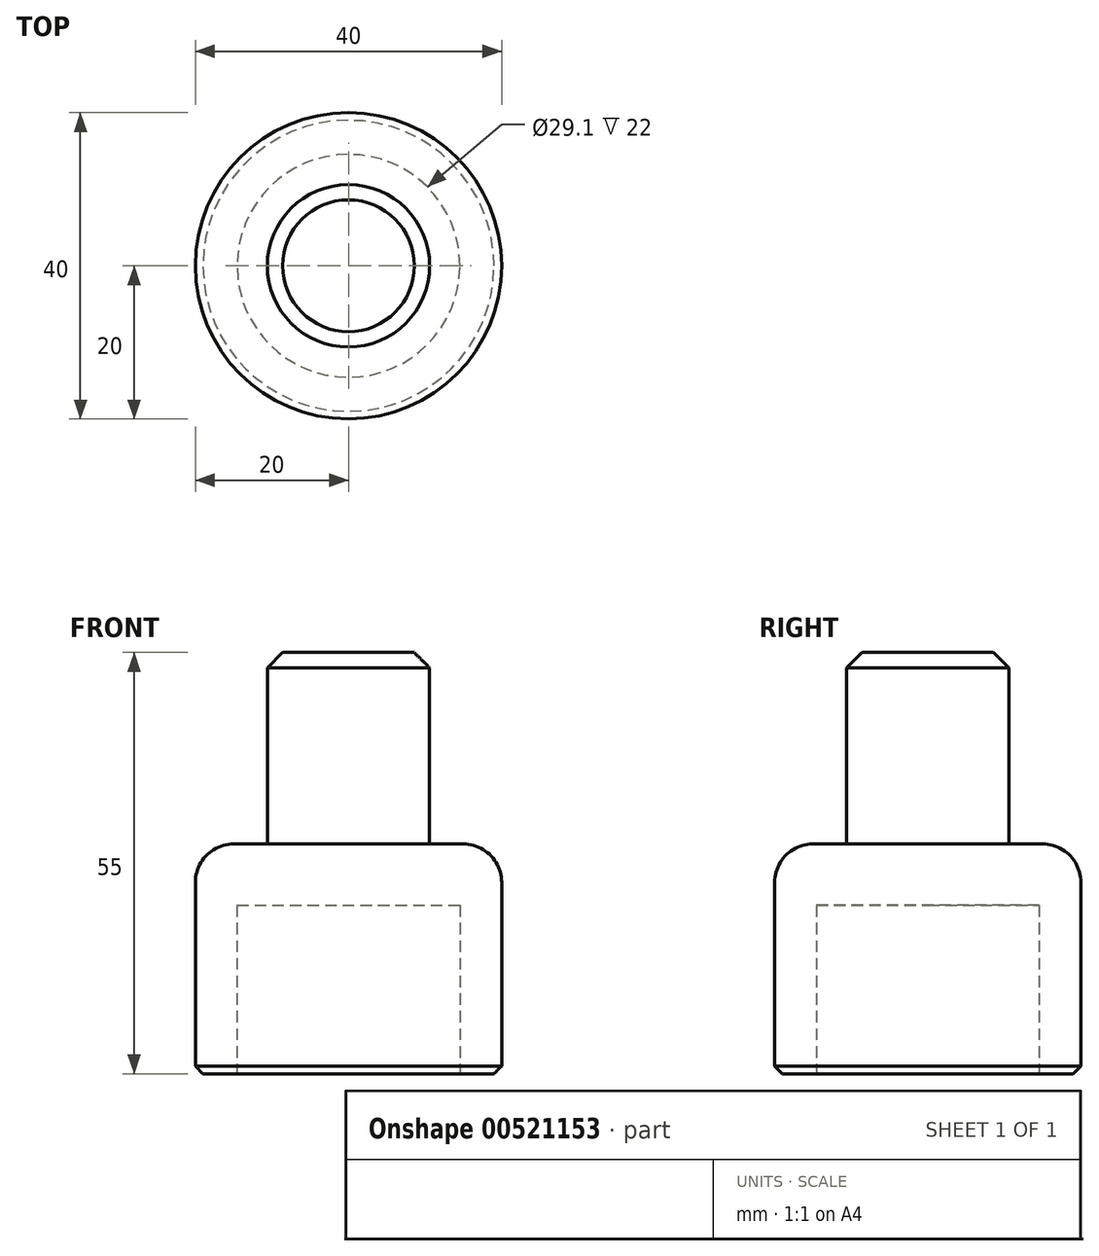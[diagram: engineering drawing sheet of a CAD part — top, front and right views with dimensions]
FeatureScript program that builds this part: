
annotation { "Feature Type Name" : "Feature", "Feature Type Description" : "" }
export const myFeature = defineFeature(function(context is Context, id is Id, definition is map)
    precondition{}
    {
        {
            var Q0;
            Q0=qCreatedBy(makeId("Top.planeOp"),FACE);
            var sketch = newSketch(context, id + "F0", { "sketchPlane" : qUnion([Q0])});
            skCircle(sketch, "E0", {"center": v(0, 0) * mm, "radius": 20 * mm});
            skSolve(sketch);
        }
        {
            var Q0;
            Q0 = qSketchRegion(id + "F0", true);
            extrude(context, id + "F1", {"entities" : qUnion([Q0]), "oppositeDirection" : true, "depth" : 30 * mm, "offsetDistance" : 25 * mm});
        }
        {
            var Q0;
            Q0=qCreatedBy(makeId("Top.planeOp"),FACE);
            var sketch = newSketch(context, id + "F2", { "sketchPlane" : qUnion([Q0])});
            skCircle(sketch, "E1", {"center": v(0, 0) * mm, "radius": 10.6 * mm});
            skSolve(sketch);
        }
        {
            var Q0;
            Q0 = qSketchRegion(id + "F2", true);
            extrude(context, id + "F3", {"entities" : qUnion([Q0]), "depth" : 25 * mm, "offsetDistance" : 25 * mm});
        }
        {
            var Q0;
            Q0=makeQuery(id+"F1.opExtrude","CAP_FACE",FACE,{"disambiguationData":[OSD([sQuery(id+"F0.wireOp",EDGE,"E0")])],"isStart":false});
            cPlane(context, id + "F4", {"entities" : qUnion([Q0]), "cplaneType" : CPlaneType.OFFSET, "offset" : 0 * mm, "width" : 150 * mm, "height" : 150 * mm});
        }
        {
            var Q0;
            Q0=qCreatedBy(id+"F4.planeOp",FACE);
            var sketch = newSketch(context, id + "F5", { "sketchPlane" : qUnion([Q0])});
            skCircle(sketch, "E2", {"center": v(0, 0) * mm, "radius": 14.55 * mm});
            skSolve(sketch);
        }
        {
            var Q0;
            Q0 = qSketchRegion(id + "F5", true);
            extrude(context, id + "F6", {"entities" : qUnion([Q0]), "operationType" : NewBodyOperationType.REMOVE, "oppositeDirection" : true, "depth" : 22 * mm, "offsetDistance" : 25 * mm});
        }
        {
            var Q0;
            Q0=makeQuery(id+"F3.opExtrude","CAP_EDGE",EDGE,{"disambiguationData":[OSD([sQuery(id+"F2.wireOp",EDGE,"E1")])],"isStart":false});
            chamfer(context, id + "F7", {"entities" : qUnion([Q0]), "width" : 2 * mm, "tangentPropagation" : true});
        }
        {
            var Q0;
            Q0=makeQuery(id+"F1.opExtrude","CAP_EDGE",EDGE,{"disambiguationData":[OSD([sQuery(id+"F0.wireOp",EDGE,"E0")])],"isStart":true});
            fillet(context, id + "F8", {"entities" : qUnion([Q0]), "radius" : 5 * mm, "tangentPropagation" : true, "allowEdgeOverflow" : false});
        }
        {
            var Q0;
            Q0=makeQuery(id+"F1.opExtrude","CAP_EDGE",EDGE,{"disambiguationData":[OSD([sQuery(id+"F0.wireOp",EDGE,"E0")])],"isStart":false});
            var Q1;
            Q1=makeQuery(id+"F6.boolean.opBoolean","COPY",EDGE,{"derivedFrom":makeQuery(id+"F6.opExtrude","CAP_EDGE",EDGE,{"disambiguationData":[OSD([sQuery(id+"F5.wireOp",EDGE,"E2")])],"isStart":true})});
            chamfer(context, id + "F9", {"entities" : qUnion([Q0, Q1]), "width" : 1 * mm, "tangentPropagation" : true});
        }
    });
